# Revit family: Sanitary_Taps&Mixers_Zurn_Z831R1-XL
name_source: partatom
category: Plumbing Fixtures
units: mm (PartAtom-declared; Revit-internal decimal feet)

## family parameters
Cut with Voids When Loaded = No
Host = Face
Maintain Annotation Orientation = No
OmniClass Number = 23.45.55.17
OmniClass Title = Mixing Faucets
Part Type = Normal
Room Calculation Point = No
Round Connector Dimension = Use Radius
Shared = No

## types (9) — shared parameters
ADA Compliance = Yes
Assembly Code = D2010
CW Connection = Yes
CWFU = 1
Default Elevation = 34"
Description = Widespread Faucet with 5 inch cast spout and lever handles
Distance B/W Base & Aerator = 2"
Distance Between Centerset = 8"
HW Connection = Yes
HWFU = 1
Inlet Connection Size (inch) = 1/2"
Lead-Free Compliant = Yes
Main Material = Brass_Zurn_Chrome Polished
Manufacturer = Zurn Water, LLC
Manufacturer Brand = Zurn
Model = Z831R1-XL
Modified Date = 09/09/2025
Product Documentation Link = https://files.zurn.com
Product Installation Sheet URL = http://www.zurn.com
Product Page URL = https://www.zurn.com
Product data URL = https://bimobject.com
Repair Parts URL = http://www.zurn.com
Spout Reach = 5"
Spout Width = 2"
URL = http://www.zurn.com
Vent Connection = No
Waste Connection = No
Width of Handle = 2 1/2"
zero-valued in all types: WFU

## per-type parameters (varying)
| type | Flow Rate | Type of Outlet | Water Sense Compliance |
| Z831R1-XL-2M (2.2 GPM AERATOR OUTLET) | 2 GPM | AERATOR | No |
| Z831R1-XL-3M (0.5 GPM SPRAY OUTLET) | 1 GPM | SPRAY | No |
| Z831R1-XL-4M (2.2 GPM LAMINAR OUTLET) | 2 GPM | LAMINAR | No |
| Z831R1-XL-7M (1.0 GPM SPRAY OUTLET) | 1 GPM | SPRAY | Yes |
| Z831R1-XL-16M (1.0 GPM SPRAY OUTLET) | 1 GPM | SPRAY | No |
| Z831R1-XL-17M (1.5 GPM AERATOR OUTLET) | 2 GPM | AERATOR | Yes |
| Z831R1-XL-18M (1.5 GPM LAMINAR OUTLET) | 2 GPM | LAMINAR | Yes |
| Z831R1-XL-22M (1.0 GPM LAMINAR OUTLET) | 1 GPM | LAMINAR | No |
| Z831R1-XL-25M (0.35 GPM SPRAY OUTLET) | 0 GPM | SPRAY | No |

## geometry (parser evidence)
native form markers: Blend x4, Sweep x4
no freeform markers — native parametric forms only
